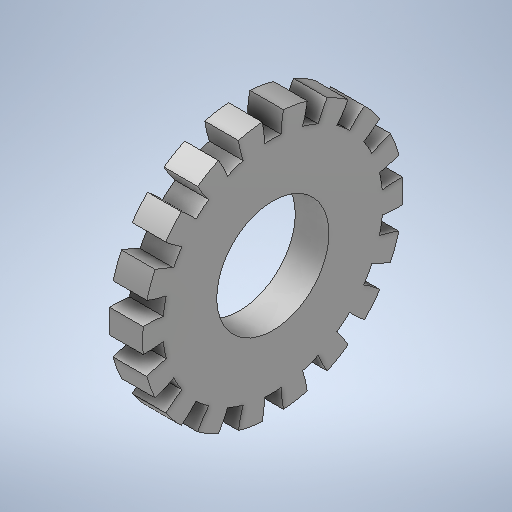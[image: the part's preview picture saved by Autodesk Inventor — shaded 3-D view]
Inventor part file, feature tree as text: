
AUTODESK INVENTOR PART (.ipt)
format: ipt  version: 2025.2 (Build 292293000, 293)  size: 364,544 bytes
history: native  units: in
note: dims shown in document units (in); Inventor stores cm internally (conversion verified against a paired STEP export)
features: other x4, extrude x1, pattern_circular x1
ambient origin geometry x8: Origin, YZ Plane, XZ Plane, XY Plane, X Axis, Y Axis, Z Axis, Center Point
bodies: Volumenkörper1 (feature_tree)
feature tree (6):
  other  "Skelett_Laufkatze.ipt"
  other  "Zahnrad_Rohling"
  extrude  "Zahngeometrie"  Depth=0.3937in
  pattern_circular  "Anzahl_zähne"  Angle=90.0deg  [1 undecoded]
  other  "Zahnrad_Laufrad_seite"
  other  "Zahnrad_Laufrad_front"
note: 1 required parameter value undecoded (feature->parameter linkage not recoverable at this tier; creation-order binding heuristic only, values carry confidence <= 0.55)
